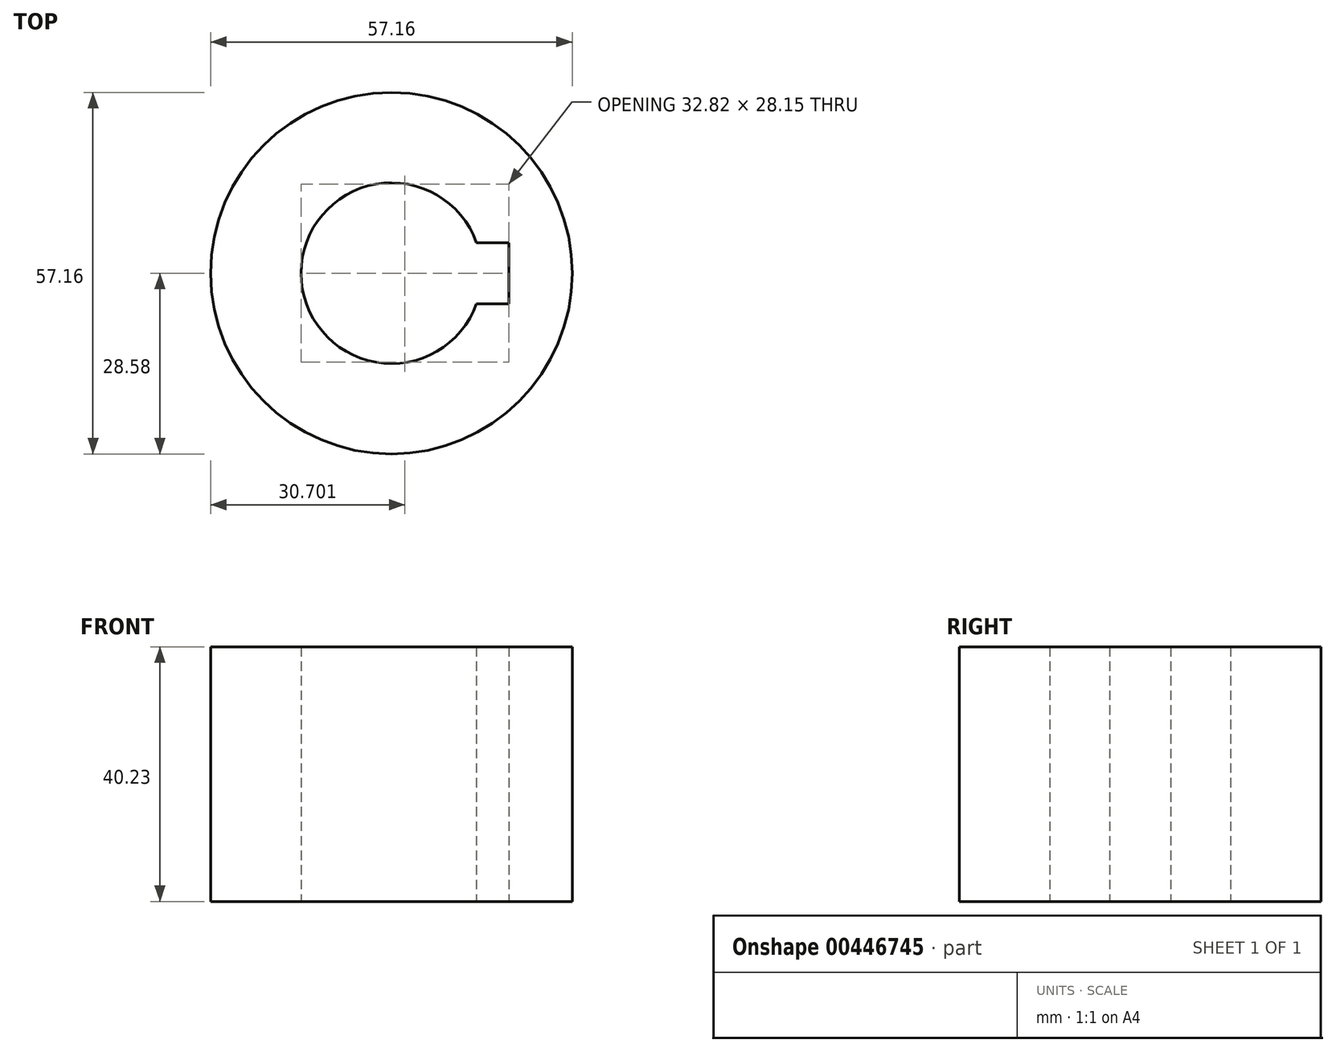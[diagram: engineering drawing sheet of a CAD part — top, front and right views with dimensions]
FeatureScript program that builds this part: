
annotation { "Feature Type Name" : "Feature", "Feature Type Description" : "" }
export const myFeature = defineFeature(function(context is Context, id is Id, definition is map)
    precondition{}
    {
        {
            var Q0;
            Q0=qCreatedBy(makeId("Top.planeOp"),FACE);
            var sketch = newSketch(context, id + "F0", { "sketchPlane" : qUnion([Q0])});
            skArc(sketch, "E0", {"start": v(13.45, 4.83) * mm, "mid": v(-14.29, 0) * mm, "end": v(13.45, -4.83) * mm});
            skCircle(sketch, "E1", {"center": v(53.98, 0) * mm, "radius": 10.16 * mm});
            skArc(sketch, "E2", {"start": v(57.34, -18.75) * mm, "mid": v(73.03, 0) * mm, "end": v(57.34, 18.75) * mm});
            skCircle(sketch, "E3", {"center": v(0, 0) * mm, "radius": 28.58 * mm});
            skLineSegment(sketch, "E4", {"start": v(5.04, 28.13) * mm, "end": v(57.34, 18.75) * mm});
            skLineSegment(sketch, "E5", {"start": v(5.04, -28.13) * mm, "end": v(57.34, -18.75) * mm});
            skLineSegment(sketch, "E6.bottom", {"start": v(13.45, 4.83) * mm, "end": v(18.53, 4.83) * mm});
            skLineSegment(sketch, "E6.top", {"start": v(13.45, -4.83) * mm, "end": v(18.53, -4.83) * mm});
            skLineSegment(sketch, "E6.right", {"start": v(18.53, 4.83) * mm, "end": v(18.53, -4.83) * mm});
            skSolve(sketch);
        }
        {
            var Q0;
            Q0=makeQuery(id+"F0.imprint","IMPRINT",FACE,{"disambiguationData":[TD([[makeQuery(id+"F0.imprint","IMPRINT",EDGE,{"derivedFrom":sQuery(id+"F0.wireOp",EDGE,"E0")}),-1.0]])]});
            extrude(context, id + "F1", {"entities" : qUnion([Q0]), "depth" : 40.23 * mm});
        }
    });
